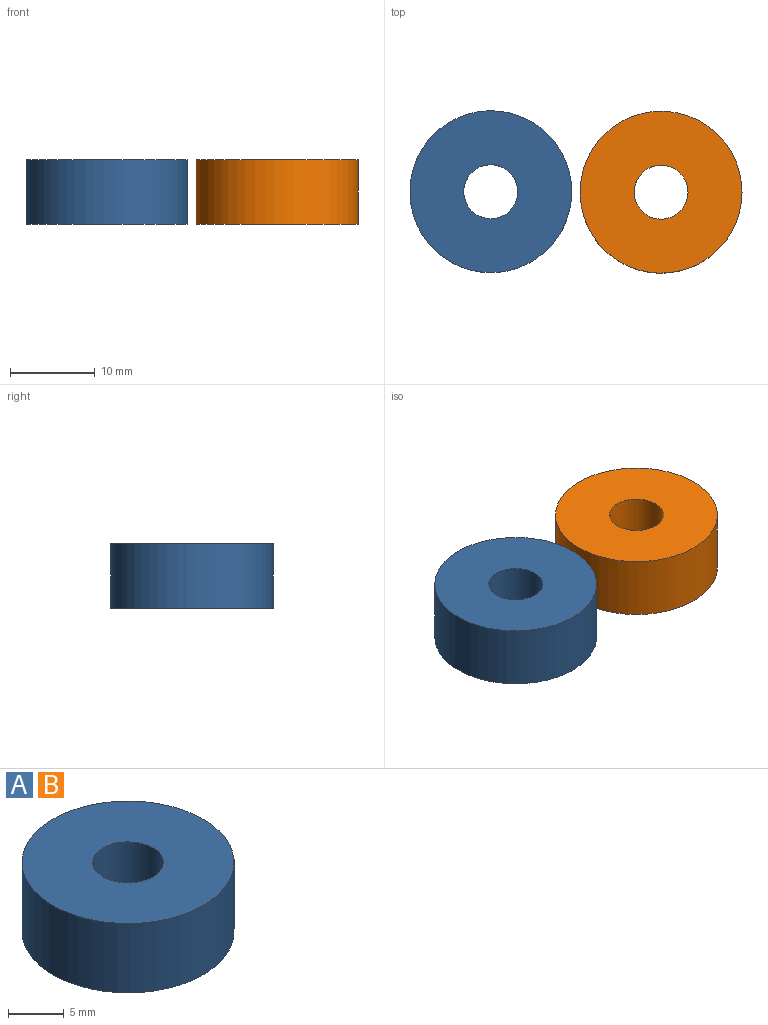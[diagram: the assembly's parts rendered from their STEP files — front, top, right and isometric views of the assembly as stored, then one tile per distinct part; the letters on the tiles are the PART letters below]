
ASSEMBLY  parts=2 mates=1
PART A: 4 faces, bbox 19.1x19.1x7.6 mm
  f0: cylinder r=3.17mm len=7.62mm, axis (0,0,-1), area 152mm2, adj f2,f3
  f1: cylinder r=9.53mm len=19.05mm, axis (0,0,-1), area 456mm2, adj f2,f3
  f2: plane 19.05x19.05mm, normal (0,0,1), area 253.4mm2, adj f0,f1
  f3: plane 19.05x19.05mm, normal (0,0,-1), area 253.4mm2, adj f0,f1
PART B: same geometry as A
PLACE A t=(1.28,2.83,-4.96)mm
PLACE B t=(21.31,2.77,-4.96)mm
MATE planar A.f1 <-> B.f1  axis (0,0,1) through (1.28,2.83,2.66)mm
